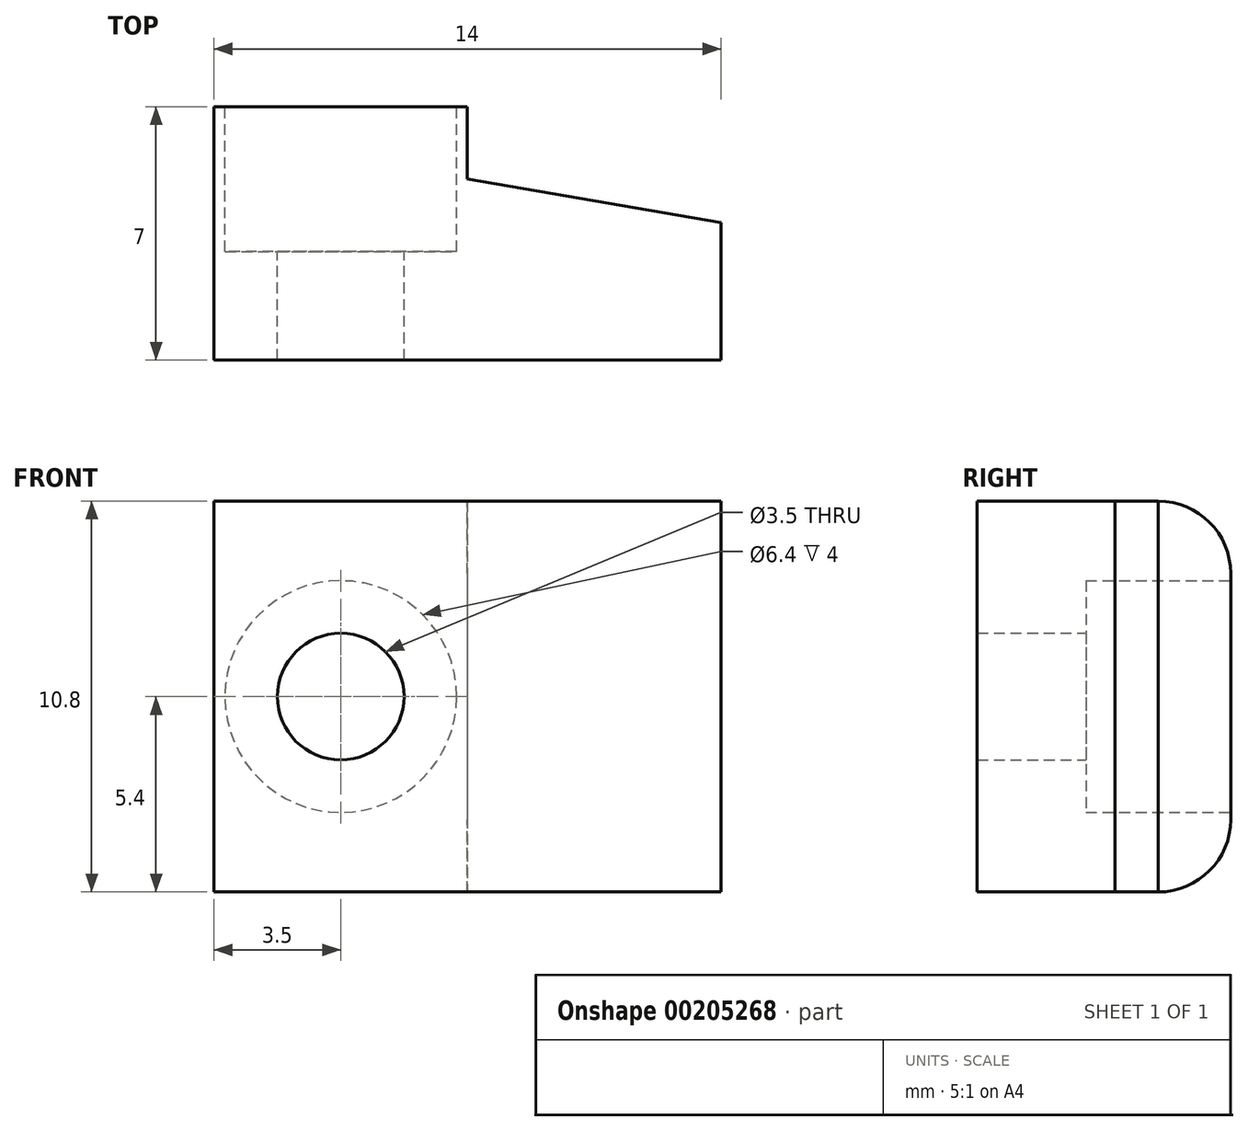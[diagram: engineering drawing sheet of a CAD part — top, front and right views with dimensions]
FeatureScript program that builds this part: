
annotation { "Feature Type Name" : "Feature", "Feature Type Description" : "" }
export const myFeature = defineFeature(function(context is Context, id is Id, definition is map)
    precondition{}
    {
        {
            var Q0;
            Q0=qCreatedBy(makeId("Top.planeOp"),FACE);
            var sketch = newSketch(context, id + "F0", { "sketchPlane" : qUnion([Q0])});
            skLineSegment(sketch, "E0", {"start": v(-7, 0) * mm, "end": v(-7, 7) * mm});
            skLineSegment(sketch, "E1", {"start": v(-7, 7) * mm, "end": v(0, 7) * mm});
            skLineSegment(sketch, "E2", {"start": v(0, 7) * mm, "end": v(0, 5) * mm});
            skLineSegment(sketch, "E3", {"start": v(0, 5) * mm, "end": v(7, 3.8) * mm});
            skLineSegment(sketch, "E4", {"start": v(7, 3.8) * mm, "end": v(7, 0) * mm});
            skLineSegment(sketch, "E5", {"start": v(7, 0) * mm, "end": v(-7, 0) * mm});
            skSolve(sketch);
        }
        {
            var Q0;
            Q0 = qSketchRegion(id + "F0", true);
            extrude(context, id + "F1", {"entities" : qUnion([Q0]), "depth" : 10.8 * mm});
        }
        {
            var Q0;
            Q0=makeQuery(id+"F1.opExtrude","SWEPT_FACE",FACE,{"disambiguationData":[OSD([sQuery(id+"F0.wireOp",EDGE,"E1")])]});
            var sketch = newSketch(context, id + "F2", { "sketchPlane" : qUnion([Q0])});
            skCircle(sketch, "E6", {"center": v(3.5, 5.4) * mm, "radius": 1.75 * mm});
            skPoint(sketch, "E6.centerSnap0", {"position": v(7, 5.4) * mm});
            skLineSegment(sketch, "E7", {"start": v(3.5, -2) * mm, "end": v(3.5, 13.16) * mm, "construction": true});
            skSolve(sketch);
        }
        {
            var Q0;
            Q0 = qSketchRegion(id + "F2", true);
            extrude(context, id + "F3", {"entities" : qUnion([Q0]), "operationType" : NewBodyOperationType.REMOVE, "endBound" : BoundingType.THROUGH_ALL, "oppositeDirection" : true, "depth" : 25 * mm});
        }
        {
            var Q0;
            Q0=makeQuery(id+"F1.opExtrude","SWEPT_FACE",FACE,{"disambiguationData":[OSD([sQuery(id+"F0.wireOp",EDGE,"E1")])]});
            var sketch = newSketch(context, id + "F4", { "sketchPlane" : qUnion([Q0])});
            skCircle(sketch, "E8", {"center": v(3.5, 5.4) * mm, "radius": 3.2 * mm});
            skSolve(sketch);
        }
        {
            var Q0;
            Q0 = qSketchRegion(id + "F4", true);
            extrude(context, id + "F5", {"entities" : qUnion([Q0]), "operationType" : NewBodyOperationType.REMOVE, "oppositeDirection" : true, "depth" : 4 * mm});
        }
        {
            var Q0;
            Q0=makeQuery(id+"F1.opExtrude","CAP_EDGE",EDGE,{"disambiguationData":[OSD([sQuery(id+"F0.wireOp",EDGE,"E1")])],"isStart":false});
            var Q1;
            Q1=makeQuery(id+"F1.opExtrude","CAP_EDGE",EDGE,{"disambiguationData":[OSD([sQuery(id+"F0.wireOp",EDGE,"E1")])],"isStart":true});
            fillet(context, id + "F6", {"entities" : qUnion([Q0, Q1]), "radius" : 2 * mm, "tangentPropagation" : true, "allowEdgeOverflow" : false});
        }
    });
